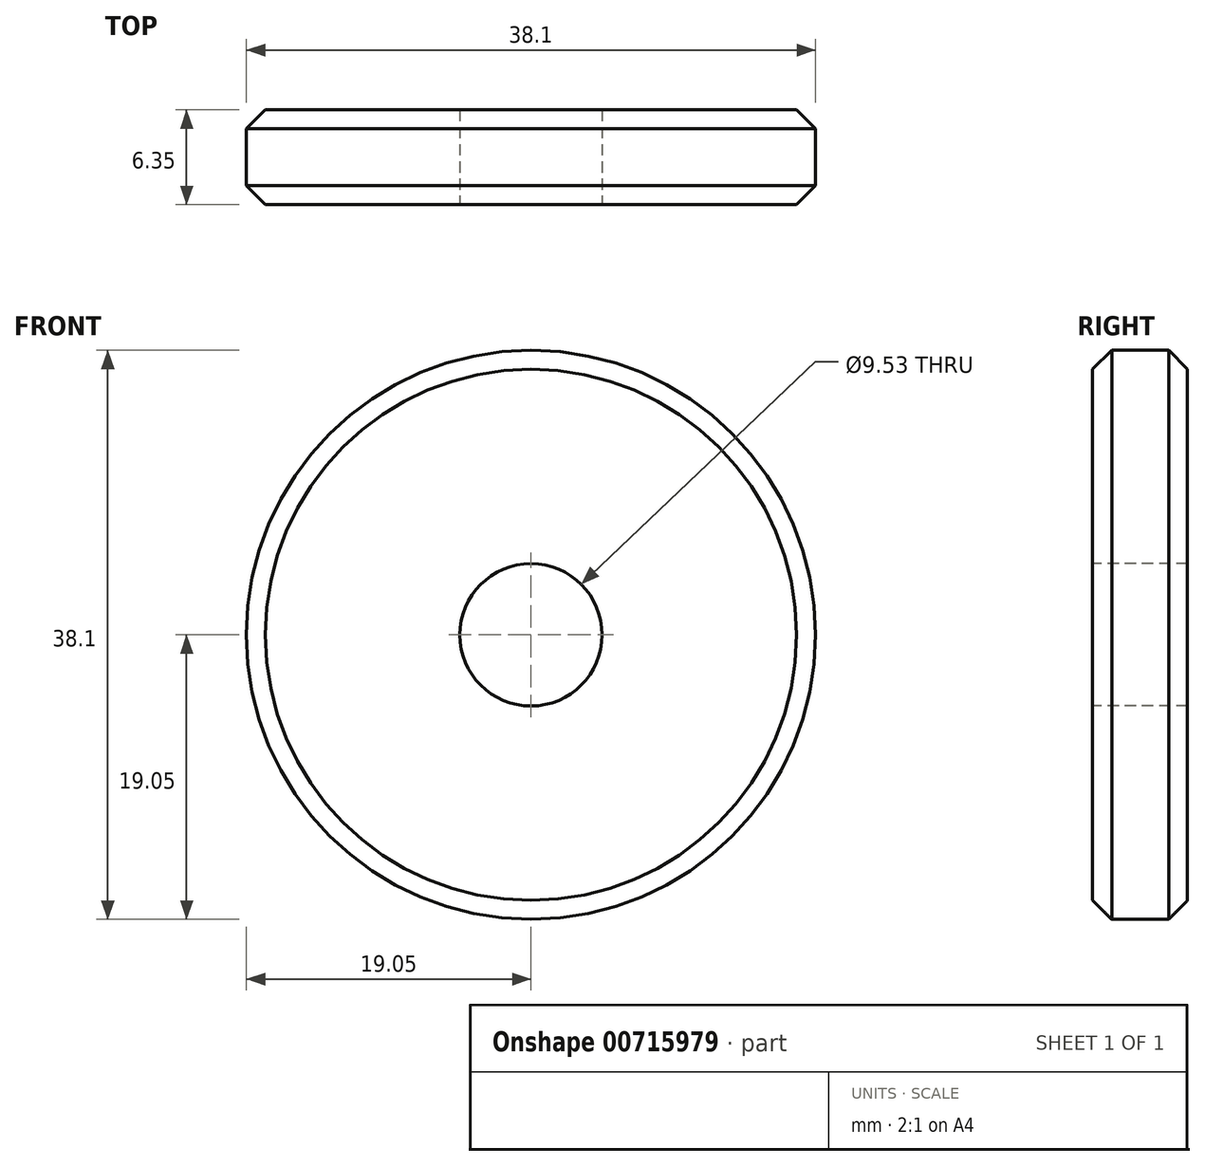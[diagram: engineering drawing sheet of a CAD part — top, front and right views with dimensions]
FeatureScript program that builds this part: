
annotation { "Feature Type Name" : "Feature", "Feature Type Description" : "" }
export const myFeature = defineFeature(function(context is Context, id is Id, definition is map)
    precondition{}
    {
        {
            var Q0;
            Q0=qCreatedBy(makeId("Front.planeOp"),FACE);
            var sketch = newSketch(context, id + "F0", { "sketchPlane" : qUnion([Q0])});
            skCircle(sketch, "E0", {"center": v(0, 0) * mm, "radius": 4.76 * mm});
            skCircle(sketch, "E1", {"center": v(0, 0) * mm, "radius": 19.05 * mm});
            skSolve(sketch);
        }
        {
            var Q0;
            Q0 = qSketchRegion(id + "F0", true);
            extrude(context, id + "F1", {"entities" : qUnion([Q0]), "oppositeDirection" : true, "depth" : 6.35 * mm, "offsetDistance" : 25.4 * mm});
        }
        {
            var Q0;
            Q0=makeQuery(id+"F1.opExtrude","CAP_EDGE",EDGE,{"disambiguationData":[OSD([sQuery(id+"F0.wireOp",EDGE,"E1")])],"isStart":true});
            var Q1;
            Q1=makeQuery(id+"F1.opExtrude","CAP_EDGE",EDGE,{"disambiguationData":[OSD([sQuery(id+"F0.wireOp",EDGE,"E1")])],"isStart":false});
            chamfer(context, id + "F2", {"entities" : qUnion([Q0, Q1]), "width" : 1.27 * mm, "tangentPropagation" : true});
        }
    });
